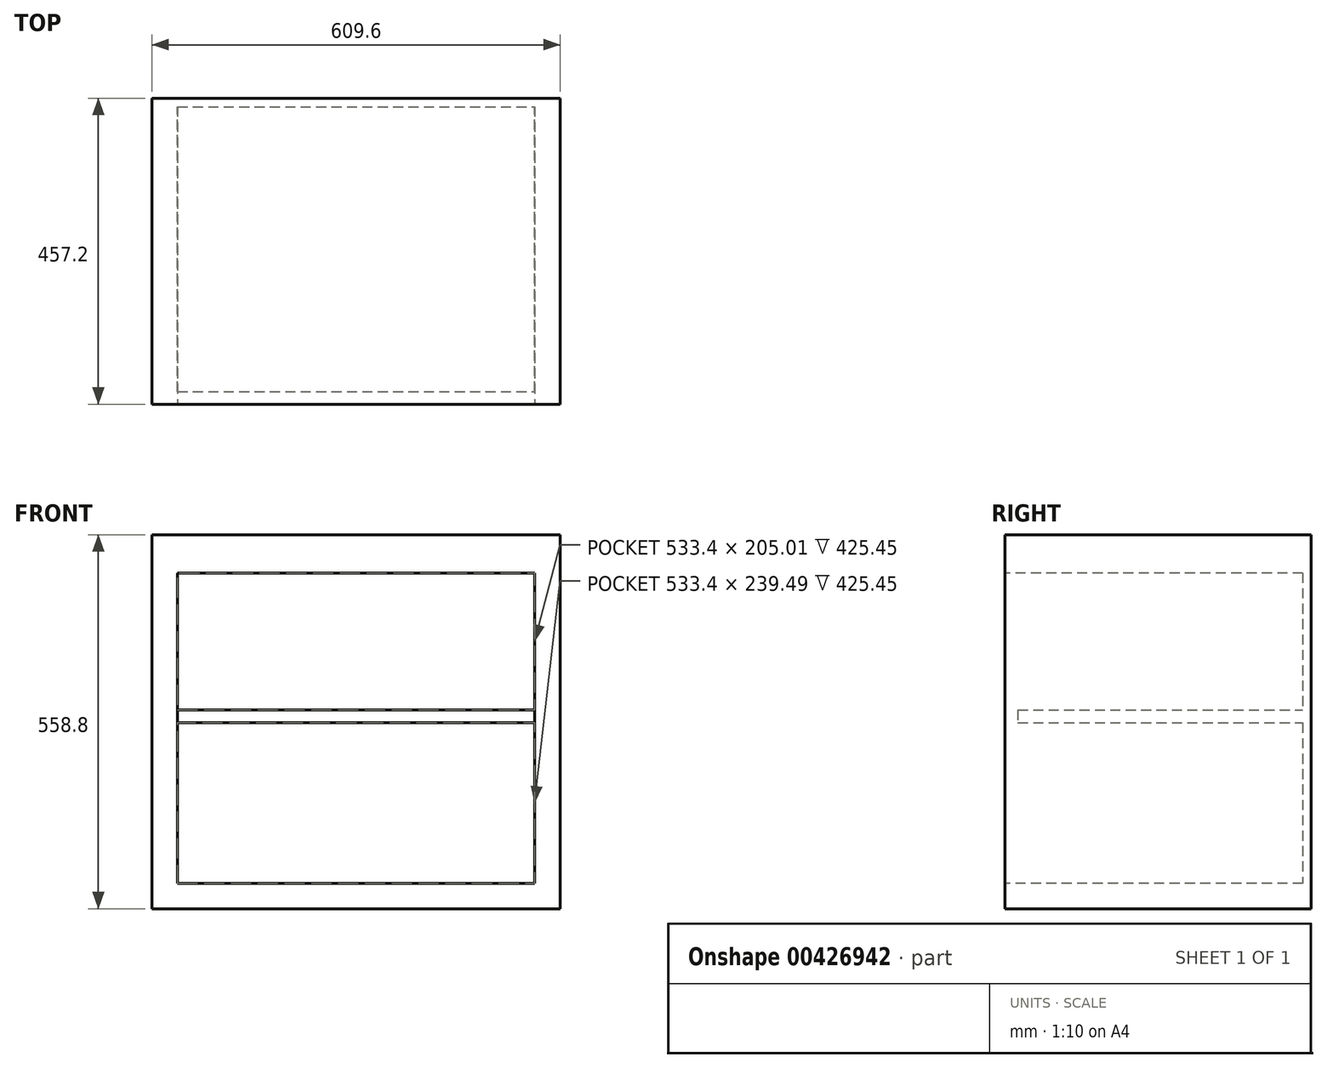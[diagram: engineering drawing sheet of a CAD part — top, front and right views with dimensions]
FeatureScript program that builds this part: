
annotation { "Feature Type Name" : "Feature", "Feature Type Description" : "" }
export const myFeature = defineFeature(function(context is Context, id is Id, definition is map)
    precondition{}
    {
        {
            var Q0;
            Q0=qCreatedBy(makeId("Right.planeOp"),FACE);
            var sketch = newSketch(context, id + "F0", { "sketchPlane" : qUnion([Q0])});
            skLineSegment(sketch, "E0.bottom", {"start": v(0, 0) * mm, "end": v(-457.2, 0) * mm});
            skLineSegment(sketch, "E0.top", {"start": v(0, 558.8) * mm, "end": v(-457.2, 558.8) * mm});
            skLineSegment(sketch, "E0.left", {"start": v(0, 0) * mm, "end": v(0, 558.8) * mm});
            skLineSegment(sketch, "E0.right", {"start": v(-457.2, 0) * mm, "end": v(-457.2, 558.8) * mm});
            skSolve(sketch);
        }
        {
            var Q0;
            Q0=makeQuery(id+"F0.imprint","IMPRINT",FACE,{"disambiguationData":[TD([[makeQuery(id+"F0.imprint","IMPRINT",EDGE,{"derivedFrom":sQuery(id+"F0.wireOp",EDGE,"E0.bottom")}),-1.0]])]});
            extrude(context, id + "F1", {"entities" : qUnion([Q0]), "depth" : 609.6 * mm});
        }
        {
            var Q0;
            Q0=makeQuery(id+"F1.opExtrude","SWEPT_FACE",FACE,{"disambiguationData":[OSD([sQuery(id+"F0.wireOp",EDGE,"E0.right")])]});
            var sketch = newSketch(context, id + "F2", { "sketchPlane" : qUnion([Q0])});
            skLineSegment(sketch, "E1.bottom", {"start": v(38.1, 501.65) * mm, "end": v(571.5, 501.65) * mm});
            skLineSegment(sketch, "E1.top", {"start": v(38.1, 38.1) * mm, "end": v(571.5, 38.1) * mm});
            skLineSegment(sketch, "E1.left", {"start": v(38.1, 501.65) * mm, "end": v(38.1, 38.1) * mm});
            skLineSegment(sketch, "E1.right", {"start": v(571.5, 501.65) * mm, "end": v(571.5, 38.1) * mm});
            skSolve(sketch);
        }
        {
            var Q0;
            Q0=makeQuery(id+"F2.imprint","IMPRINT",FACE,{"disambiguationData":[TD([[makeQuery(id+"F2.imprint","IMPRINT",EDGE,{"derivedFrom":sQuery(id+"F2.wireOp",EDGE,"E1.bottom")}),-1.0]])]});
            extrude(context, id + "F3", {"entities" : qUnion([Q0]), "operationType" : NewBodyOperationType.REMOVE, "oppositeDirection" : true, "depth" : 444.5 * mm});
        }
        {
            var Q0;
            Q0=makeQuery(id+"F3.boolean.opBoolean","COPY",FACE,{"derivedFrom":makeQuery(id+"F3.opExtrude","CAP_FACE",FACE,{"disambiguationData":[OSD([sQuery(id+"F2.wireOp",EDGE,"E1.bottom"),sQuery(id+"F2.wireOp",EDGE,"E1.top"),sQuery(id+"F2.wireOp",EDGE,"E1.left"),sQuery(id+"F2.wireOp",EDGE,"E1.right")])],"isStart":false})});
            var sketch = newSketch(context, id + "F4", { "sketchPlane" : qUnion([Q0])});
            skLineSegment(sketch, "E2.bottom", {"start": v(38.1, 296.64) * mm, "end": v(571.5, 296.64) * mm});
            skLineSegment(sketch, "E2.top", {"start": v(38.1, 277.6) * mm, "end": v(571.5, 277.6) * mm});
            skLineSegment(sketch, "E2.left", {"start": v(38.1, 296.64) * mm, "end": v(38.1, 277.6) * mm});
            skLineSegment(sketch, "E2.right", {"start": v(571.5, 296.64) * mm, "end": v(571.5, 277.6) * mm});
            skSolve(sketch);
        }
        {
            var Q0;
            Q0=makeQuery(id+"F4.imprint","IMPRINT",FACE,{"disambiguationData":[TD([[makeQuery(id+"F4.imprint","IMPRINT",EDGE,{"derivedFrom":sQuery(id+"F4.wireOp",EDGE,"E2.bottom")}),-1.0]])]});
            var Q1;
            Q1=makeQuery(id+"F4.imprint","IMPRINT",FACE,{"disambiguationData":[TD([[makeQuery(id+"F4.imprint","IMPRINT",EDGE,{"derivedFrom":sQuery(id+"F4.wireOp",EDGE,"bMyBUHrY-iDEY-2QoT-N59H-OzIF14o39hIS.bottom")}),-1.0]])]});
            extrude(context, id + "F5", {"entities" : qUnion([Q0, Q1]), "operationType" : NewBodyOperationType.ADD, "depth" : 425.45 * mm});
        }
    });
